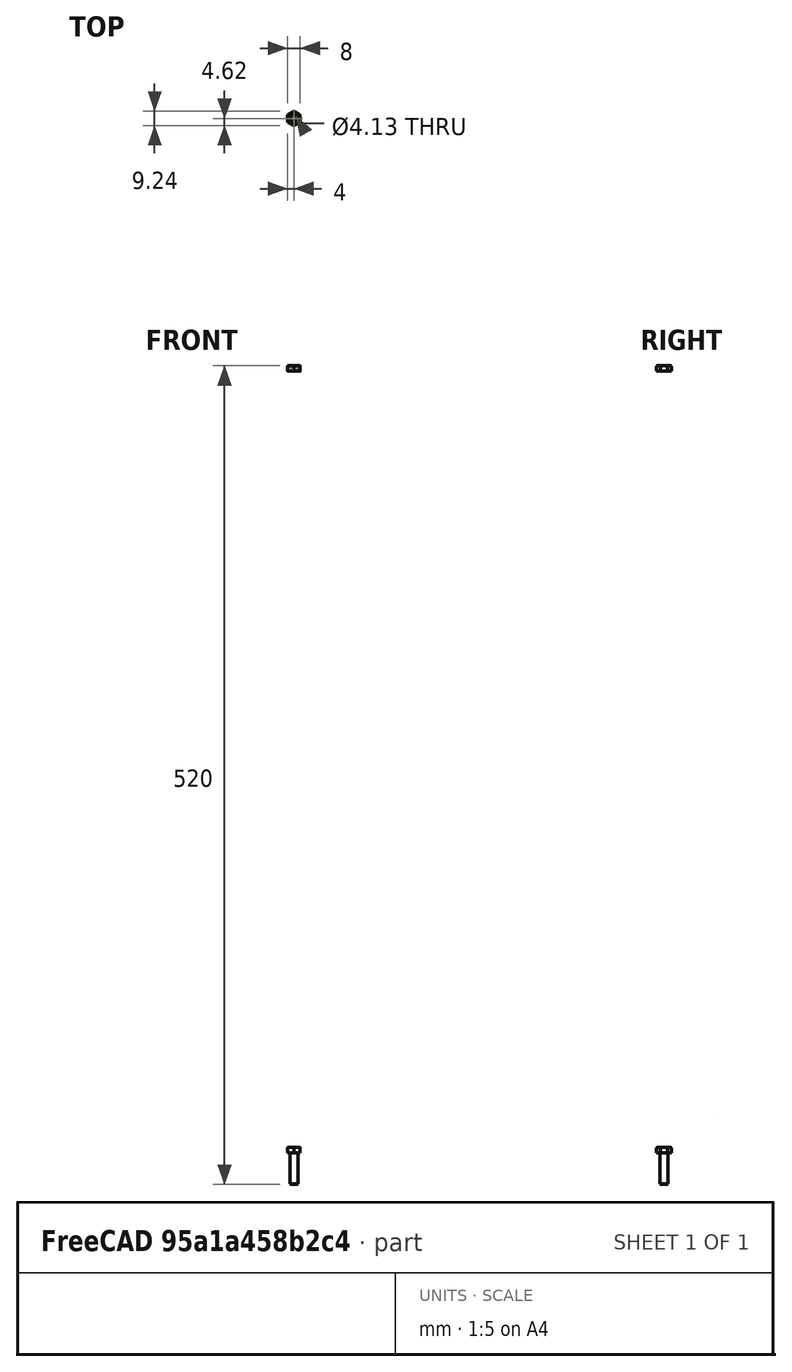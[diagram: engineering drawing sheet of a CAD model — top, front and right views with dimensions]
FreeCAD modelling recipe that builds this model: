
FCSTD DOCUMENT  (FreeCAD 0.19R24276 (Git))
Label: v5.6_Pole
License: All rights reserved
LicenseURL: http://en.wikipedia.org/wiki/All_rights_reserved
objects: PartDesign::CoordinateSystem×3, App::Link×3, App::DocumentObjectGroup×2, Part::FeaturePython×2, App::FeaturePython×1, App::Part×1
note: 5 computed .brp shape members not serialized (recipe doc carries the construction recipe); baked Part::Feature solids carry a one-line shape summary decoded from their .brp
EXTERNAL_REF file=v5.6_Master.FCStd obj=Local_CS040
EXTERNAL_REF file=v5.6_Master.FCStd obj=Body015
EXTERNAL_REF file=v5.6_Master.FCStd obj=Local_CS204
EXTERNAL_REF file=v5.6_Master.FCStd obj=Body022015
EXTERNAL_REF file=v5.6_Master.FCStd obj=Local_CS199
EXTERNAL_REF file=v5.6_Master.FCStd obj=Local_CS202
EXTERNAL_REF file=v5.6_Master.FCStd obj=Local_CS203

FEATURE [App::DocumentObjectGroup] Parts
FEATURE [PartDesign::CoordinateSystem] LCS_Origin
  AttacherType = Attacher::AttachEngine3D
  MapMode = 2
  Support = -> [X_Axis]
FEATURE [App::DocumentObjectGroup] Constraints
FEATURE [App::FeaturePython] Variables  # WARN: FeaturePython — macro-defined, semantics opaque (R4)
FEATURE [App::Link] Pole_Body
  AssemblyType = Asm4EE
  AttachedBy = #Local_CS040
  AttachedTo = Parent Assembly#LCS_Origin
  LinkPlacement = pos=(0,0,0) rot=(0,0,-1;1.5708rad)
  LinkedObject = -> <external v5.6_Master.FCStd>#Body015
  Placement = pos=(0,0,0) rot=(0,0,-1;1.5708rad)
  expr: Placement = LCS_Origin.Placement * AttachmentOffset * v5_6_Master#Local_CS040.Placement ^ -1
FEATURE [App::Link] PoleBase_Lower
  AssemblyType = Asm4EE
  AttachedBy = #Local_CS204
  AttachedTo = Pole_Body#Local_CS040
  LinkPlacement = pos=(0,0,-4) rot=(0,0,-1;1.5708rad)
  LinkedObject = -> <external v5.6_Master.FCStd>#Body022015
  Placement = pos=(0,0,-4) rot=(0,0,-1;1.5708rad)
  expr: Placement = Pole_Body.Placement * v5_6_Master#Local_CS040.Placement * AttachmentOffset * v5_6_Master#Local_CS204.Placement ^ -1
FEATURE [App::Link] PoleBase_Upper
  AssemblyType = Asm4EE
  AttachedBy = #Local_CS204
  AttachedTo = Pole_Body#Local_CS199
  LinkPlacement = pos=(0,0,504) rot=(0.707107,-0.707107,0;3.14159rad)
  LinkedObject = -> <external v5.6_Master.FCStd>#Body022015
  Placement = pos=(0,0,504) rot=(0.707107,-0.707107,0;3.14159rad)
  expr: Placement = Pole_Body.Placement * v5_6_Master#Local_CS199.Placement * AttachmentOffset * v5_6_Master#Local_CS204.Placement ^ -1
FEATURE [Part::FeaturePython] Screw  label="M5x20-Screw"  # Fasteners workbench fastener (typed FeaturePython)
  AssemblyType = Asm4EE
  AttachedBy = Origin
  AttachedTo = PoleBase_Lower#Local_CS202
  Placement = pos=(0,0,0) rot=(0,0,1;1.5708rad)
  diameter = 7
  invert = false
  length = 5
  lengthCustom = 20
  matchOuter = false
  offset = 0
  thread = false
  type = 27
  expr: Placement = PoleBase_Lower.Placement * v5_6_Master#Local_CS202.Placement * AttachmentOffset
FEATURE [Part::FeaturePython] Nut  label="M5-Nut"  # Fasteners workbench fastener (typed FeaturePython)
  AssemblyType = Asm4EE
  AttachedBy = Origin
  AttachedTo = PoleBase_Upper#Local_CS202
  Placement = pos=(0,0,500) rot=(-0.707107,-0.707107,0;3.14159rad)
  diameter = 7
  invert = false
  matchOuter = false
  offset = 0
  thread = false
  type = 7
  expr: Placement = PoleBase_Upper.Placement * v5_6_Master#Local_CS202.Placement * AttachmentOffset
FEATURE [PartDesign::CoordinateSystem] LCS_Pole_Bottom
  AttacherType = Attacher::AttachEngine3D
  Placement = pos=(0,0,-4) rot=(0,0,1;0rad)
  expr: Placement = PoleBase_Lower.Placement * v5_6_Master#Local_CS203.Placement * AttachmentOffset
FEATURE [PartDesign::CoordinateSystem] LCS_Pole_Top
  AttacherType = Attacher::AttachEngine3D
  AttachmentOffset = pos=(0,0,0) rot=(0,-1,0;3.14159rad)
  Placement = pos=(0,0,504) rot=(0,0,1;0rad)
  expr: Placement = PoleBase_Upper.Placement * v5_6_Master#Local_CS203.Placement * AttachmentOffset
FEATURE [App::Part] Model  label="Pole"
  Configuration = 0
  Group = -> [LCS_Origin,Constraints,Variables,Pole_Body,PoleBase_Lower,PoleBase_Upper,Screw,Nut,LCS_Pole_Bottom,LCS_Pole_Top]
  Origin = -> Origin
  Type = Assembly4 Model

RESOLVED EXTERNAL PARTS (link-assembly join: the EXTERNAL_REF files above that resolve inside this repo's crawl, each included once):
---- part v5.6_Master.FCStd = doc fcstd_204eddf974d0 (447149 chars; too large to inline — full recipe in that document) ----
